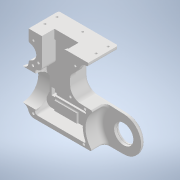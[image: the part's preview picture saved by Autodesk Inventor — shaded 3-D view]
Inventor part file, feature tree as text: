
AUTODESK INVENTOR PART (.ipt)
format: ipt  version: 2020 (Build 240168000, 168)  size: 1,025,536 bytes
history: native  units: mm
features: sketch x7, other x6, extrude x5, hole x2, projected_geometry x2, reference x1
ambient origin geometry x8: Origin, YZ Plane, XZ Plane, XY Plane, X Axis, Y Axis, Z Axis, Center Point
bodies: Solid1 (feature_tree)
feature tree (23):
  other  "bodyL.ipt"
  extrude  "Extrusion1"  Depth=52.0mm
  extrude  "Extrusion3"  Depth=10.0mm
  extrude  "Extrusion4"  Depth=32.08mm
  extrude  "Extrusion5"  Depth=31.0mm
  hole  "Hole1"  [1 undecoded]
  hole  "Hole2"  [1 undecoded]
  extrude  "Extrusion6"  [1 undecoded]
  other  "Solid1::bodyL.ipt"
  other  "TaggingFeature2"
  sketch  "Sketch1"  dims[d1=10.0mm]
  sketch  "Sketch3"  dims[d4=54.0mm d6=58.0mm d7=15.0mm d8=65.0mm d9=30.0mm d10=0.0mm d12=120.0mm d14=15.0mm d15=80.0mm d16=52.0mm d17=60.0mm d19=24.0mm d20=0.0mm d21=7.0mm d22=40.0mm d23=20.0mm d24=0.0mm d25=25.0mm d26=3.4mm d28=6.3mm d30=90.0deg d31=20.0mm d46=81.0mm d48=0.0mm d49=25.0mm d50=3.4mm d52=6.3mm d54=90.0deg d55=20.0mm d57=11.0mm d59=0.0mm d2=52.0mm]
  sketch  "Sketch4"  dims[d3=10.0mm d5=0.0mm d41=40.0mm]
  sketch  "Sketch5"  dims[d43=7.0mm d47=0.0mm d51=32.08mm]
  reference  "Reference1"
  sketch  "Sketch6"  dims[d53=7.0mm d56=0.0mm d58=31.0mm]
  projected_geometry  "Projected Loop2"
  sketch  "Sketch7"  dims[d60=2.5mm d61=0.0mm]
  projected_geometry  "Projected Loop3"
  sketch  "Sketch8"  dims[d62=3.4mm d63=6.0mm d64=6.3mm d65=2.0mm d66=90.0deg d67=8.0mm d68=20.594885mm d69=3.4mm d70=6.0mm d71=6.3mm d72=2.0mm d73=90.0deg d74=8.0mm d75=20.594885mm d76=10.0mm d77=0.0mm]
  other  "<userpath>\Desktop\KangKangBalancing\KangKang.iam"
  other  "KangKang.iam"
  other  "front wheel:1"
note: 3 required parameter values undecoded (feature->parameter linkage not recoverable at this tier; creation-order binding heuristic only, values carry confidence <= 0.55)
